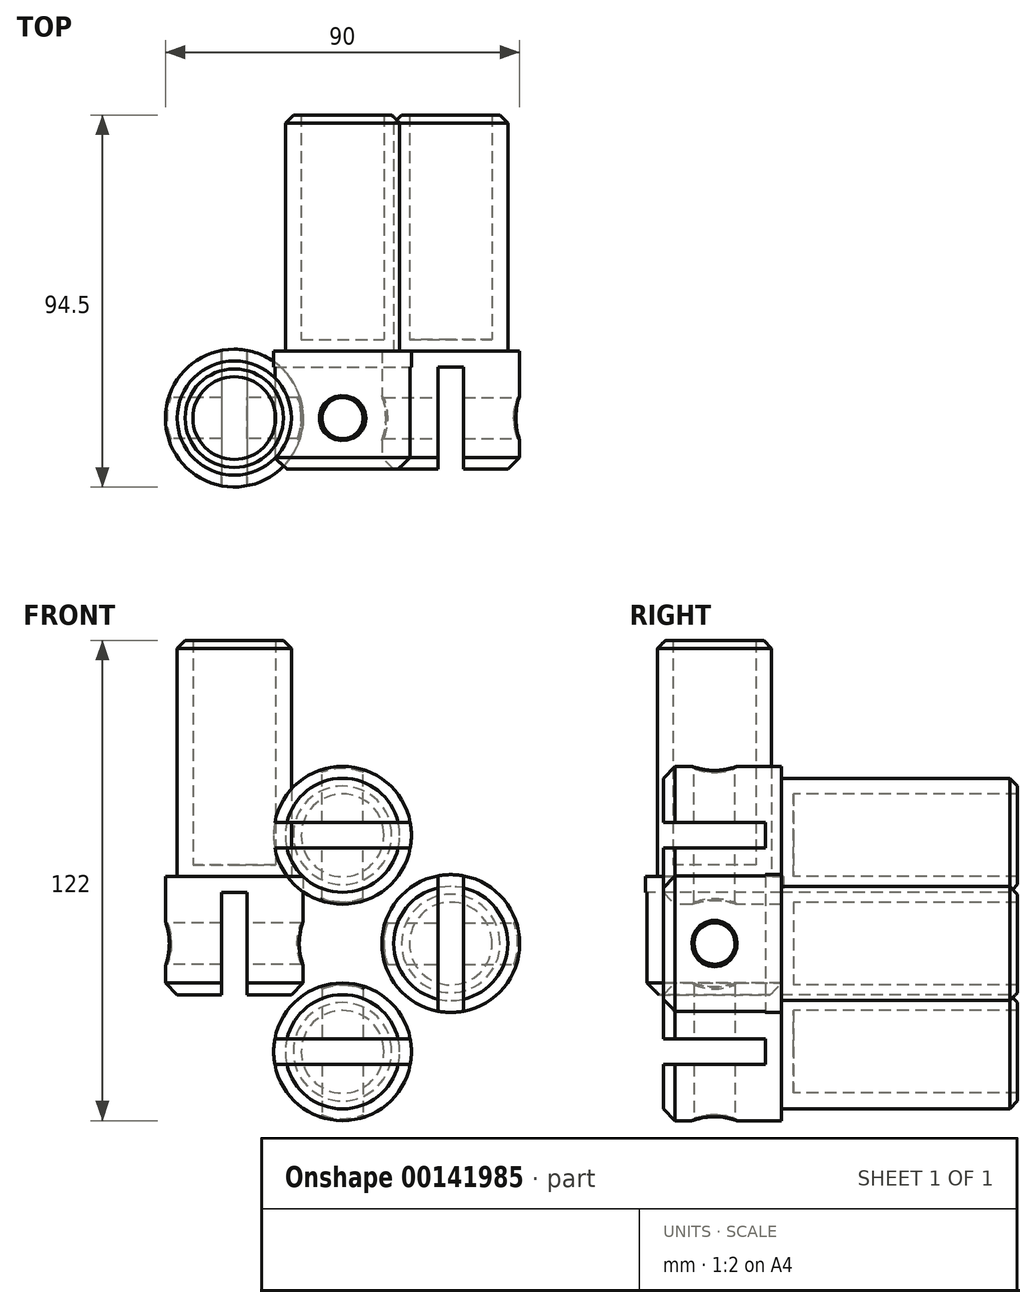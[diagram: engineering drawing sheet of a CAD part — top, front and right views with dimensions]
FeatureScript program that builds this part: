
annotation { "Feature Type Name" : "Feature", "Feature Type Description" : "" }
export const myFeature = defineFeature(function(context is Context, id is Id, definition is map)
    precondition{}
    {
        {
            var Q0;
            Q0=qCreatedBy(makeId("Top.planeOp"),FACE);
            var sketch = newSketch(context, id + "F0", { "sketchPlane" : qUnion([Q0])});
            skLineSegment(sketch, "E0", {"start": v(-14.5, 77) * mm, "end": v(0, 77) * mm});
            skLineSegment(sketch, "E1", {"start": v(-14.5, 77) * mm, "end": v(-14.5, 17) * mm});
            skLineSegment(sketch, "E2", {"start": v(-14.5, 17) * mm, "end": v(-17.5, 17) * mm});
            skLineSegment(sketch, "E3", {"start": v(-17.5, 17) * mm, "end": v(-17.5, -10) * mm});
            skLineSegment(sketch, "E4", {"start": v(-14.5, -13) * mm, "end": v(-3.25, -13) * mm});
            skLineSegment(sketch, "E5", {"start": v(-3.25, -13) * mm, "end": v(-3.25, 13) * mm});
            skLineSegment(sketch, "E6", {"start": v(-3.25, 13) * mm, "end": v(0, 13) * mm});
            skLineSegment(sketch, "E7", {"start": v(0, 13) * mm, "end": v(0, 77) * mm});
            skLineSegment(sketch, "E8", {"start": v(-17.5, -10) * mm, "end": v(-14.5, -13) * mm});
            skPoint(sketch, "E9.orphan", {"position": v(-17.5, -13) * mm});
            skLineSegment(sketch, "E10.MirrorCS", {"start": v(3.25, 13) * mm, "end": v(0, 13) * mm});
            skLineSegment(sketch, "E11.MirrorCS", {"start": v(3.25, -13) * mm, "end": v(3.25, 13) * mm});
            skLineSegment(sketch, "E12.MirrorCS", {"start": v(14.5, -13) * mm, "end": v(3.25, -13) * mm});
            skLineSegment(sketch, "E13.MirrorCS", {"start": v(17.5, -10) * mm, "end": v(14.5, -13) * mm});
            skLineSegment(sketch, "E14.MirrorCS", {"start": v(17.5, 17) * mm, "end": v(17.5, -10) * mm});
            skLineSegment(sketch, "E15.MirrorCS", {"start": v(14.5, 17) * mm, "end": v(17.5, 17) * mm});
            skLineSegment(sketch, "E16.MirrorCS", {"start": v(14.5, 77) * mm, "end": v(14.5, 17) * mm});
            skLineSegment(sketch, "E17.MirrorCS", {"start": v(14.5, 77) * mm, "end": v(0, 77) * mm});
            skLineSegment(sketch, "E18", {"start": v(-3.25, -13) * mm, "end": v(3.25, -13) * mm});
            skLineSegment(sketch, "E19", {"start": v(-10.5, 77) * mm, "end": v(-10.5, 20) * mm});
            skLineSegment(sketch, "E20", {"start": v(-10.5, 20) * mm, "end": v(10.5, 20) * mm});
            skLineSegment(sketch, "E21", {"start": v(10.5, 20) * mm, "end": v(10.5, 77) * mm});
            skLineSegment(sketch, "E22", {"start": v(-17.5, 0) * mm, "end": v(17.5, 0) * mm, "construction": true});
            skLineSegment(sketch, "E23", {"start": v(27.5, 47) * mm, "end": v(27.5, -13) * mm, "construction": true});
            skSolve(sketch);
        }
        {
            var Q0;
            {var subQ5=sQuery(id+"F0.wireOp",EDGE,"E1");Q0=makeQuery(id+"F0.imprint","IMPRINT",FACE,{"disambiguationData":[TD([[makeQuery(id+"F0.imprint","IMPRINT",EDGE,{"derivedFrom":subQ5}),1.0]])]});}
            var Q1;
            Q1=sQuery(id+"F0.wireOp",EDGE,"E7");
            revolve(context, id + "F1", {"entities" : qUnion([Q0]), "axis" : qUnion([Q1]), "revolveType" : RevolveType.FULL});
        }
        {
            var Q0;
            Q0=makeQuery(id+"F0.imprint","IMPRINT",FACE,{"disambiguationData":[TD([[makeQuery(id+"F0.imprint","IMPRINT",EDGE,{"derivedFrom":sQuery(id+"F0.wireOp",EDGE,"E5")}),-1.0]])]});
            extrude(context, id + "F2", {"entities" : qUnion([Q0]), "operationType" : NewBodyOperationType.REMOVE, "endBound" : BoundingType.SYMMETRIC, "oppositeDirection" : true, "depth" : 35 * mm});
        }
        {
            var Q0;
            Q0=qCreatedBy(makeId("Right.planeOp"),FACE);
            var sketch = newSketch(context, id + "F3", { "sketchPlane" : qUnion([Q0])});
            skCircle(sketch, "E24", {"center": v(0, 0) * mm, "radius": 5.25 * mm});
            skSolve(sketch);
        }
        {
            var Q0;
            Q0 = qSketchRegion(id + "F3", true);
            extrude(context, id + "F4", {"entities" : qUnion([Q0]), "operationType" : NewBodyOperationType.REMOVE, "endBound" : BoundingType.SYMMETRIC, "depth" : 35 * mm});
        }
        {
            var Q0;
            Q0=makeQuery(id+"F1.opRevolve","SWEPT_EDGE",EDGE,{"disambiguationData":[OSD([sQuery(id+"F0.wireOp",EDGE,"E0"),sQuery(id+"F0.wireOp",EDGE,"E1")])]});
            chamfer(context, id + "F5", {"entities" : qUnion([Q0]), "width" : 2 * mm, "tangentPropagation" : true});
        }
        {
            var Q0;
            Q0=makeQuery(id+"F4.boolean.opBoolean","INTERSECT",EDGE,{"disambiguationData":[OD(1.0)],"derivedFrom":[makeQuery(id+"F1.opRevolve","SWEPT_FACE",FACE,{"disambiguationData":[OSD([sQuery(id+"F0.wireOp",EDGE,"E3")])]}),makeQuery(id+"F4.opExtrude","SWEPT_FACE",FACE,{"disambiguationData":[OSD([sQuery(id+"F3.wireOp",EDGE,"E24")])]})]});
            var Q1;
            Q1=makeQuery(id+"F4.boolean.opBoolean","INTERSECT",EDGE,{"disambiguationData":[OD(0.0)],"derivedFrom":[makeQuery(id+"F1.opRevolve","SWEPT_FACE",FACE,{"disambiguationData":[OSD([sQuery(id+"F0.wireOp",EDGE,"E3")])]}),makeQuery(id+"F4.opExtrude","SWEPT_FACE",FACE,{"disambiguationData":[OSD([sQuery(id+"F3.wireOp",EDGE,"E24")])]})]});
            fillet(context, id + "F6", {"entities" : qUnion([Q0, Q1]), "radius" : 0.5 * mm, "tangentPropagation" : true, "allowEdgeOverflow" : false});
        }
        {
            var Q0;
            Q0=makeQuery(id+"F1.opRevolve","SWEPT_BODY",BODY,{"disambiguationData":[OSD([sQuery(id+"F0.wireOp",EDGE,"E0"),sQuery(id+"F0.wireOp",EDGE,"E1"),sQuery(id+"F0.wireOp",EDGE,"E2"),sQuery(id+"F0.wireOp",EDGE,"E3"),sQuery(id+"F0.wireOp",EDGE,"E4"),sQuery(id+"F0.wireOp",EDGE,"E5"),sQuery(id+"F0.wireOp",EDGE,"E6"),sQuery(id+"F0.wireOp",EDGE,"E7"),sQuery(id+"F0.wireOp",EDGE,"E8"),sQuery(id+"F0.wireOp",EDGE,"E19"),sQuery(id+"F0.wireOp",EDGE,"E20")])]});
            var Q1;
            Q1=sQuery(id+"F0.wireOp",EDGE,"E23");
            circularPattern(context, id + "F7", {"operationType" : NewBodyOperationType.ADD, "entities" : qUnion([Q0]), "axis" : qUnion([Q1]), "angle" : 90 * degree, "instanceCount" : 4});
        }
        {
            var Q0;
            Q0=makeQuery(id+"F1.opRevolve","SWEPT_BODY",BODY,{"disambiguationData":[OSD([sQuery(id+"F0.wireOp",EDGE,"E0"),sQuery(id+"F0.wireOp",EDGE,"E1"),sQuery(id+"F0.wireOp",EDGE,"E2"),sQuery(id+"F0.wireOp",EDGE,"E3"),sQuery(id+"F0.wireOp",EDGE,"E4"),sQuery(id+"F0.wireOp",EDGE,"E5"),sQuery(id+"F0.wireOp",EDGE,"E6"),sQuery(id+"F0.wireOp",EDGE,"E7"),sQuery(id+"F0.wireOp",EDGE,"E8"),sQuery(id+"F0.wireOp",EDGE,"E19"),sQuery(id+"F0.wireOp",EDGE,"E20")])]});
            var Q1;
            Q1=sQuery(id+"F0.wireOp",EDGE,"E22");
            transform(context, id + "F8", {"entities" : qUnion([Q0]), "transformType" : TransformType.ROTATION, "transformAxis" : qUnion([Q1]), "angle" : 90 * degree, "makeCopy" : false});
        }
    });
